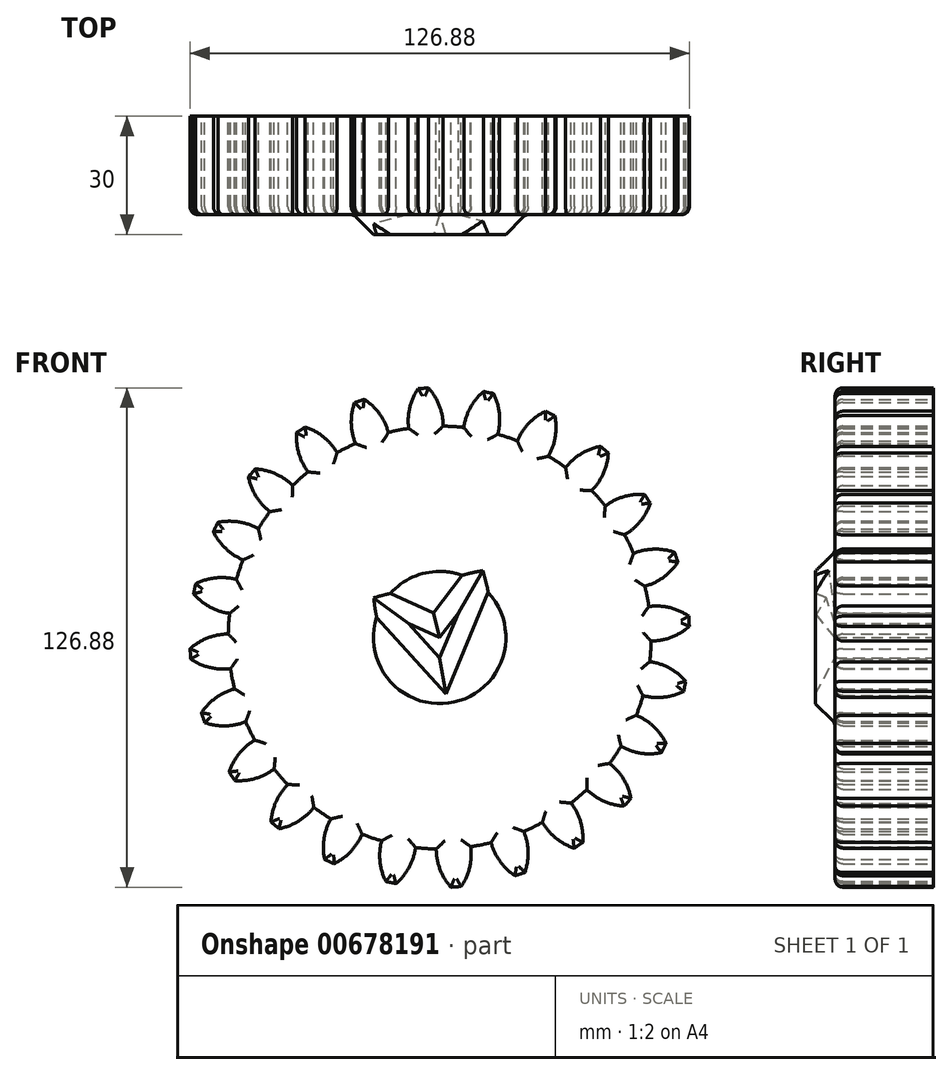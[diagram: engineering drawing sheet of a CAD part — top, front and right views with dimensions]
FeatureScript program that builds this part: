
annotation { "Feature Type Name" : "Feature", "Feature Type Description" : "" }
export const myFeature = defineFeature(function(context is Context, id is Id, definition is map)
    precondition{}
    {
        {
            var Q0;
            Q0=qCreatedBy(makeId("Front.planeOp"),FACE);
            var sketch = newSketch(context, id + "F0", { "sketchPlane" : qUnion([Q0])});
            skCircle(sketch, "E0", {"center": v(0, 0) * mm, "radius": 53.72 * mm});
            skCircle(sketch, "E1", {"center": v(0, 0) * mm, "radius": 58.67 * mm, "construction": true});
            skCircle(sketch, "E2", {"center": v(0, 0) * mm, "radius": 63.5 * mm, "construction": true});
            skLineSegment(sketch, "E3", {"start": v(0, 0) * mm, "end": v(0, 72.49) * mm, "construction": true});
            skLineSegment(sketch, "E4", {"start": v(0, 0) * mm, "end": v(-5.24, 80.02) * mm, "construction": true});
            skLineSegment(sketch, "E5", {"start": v(0, 58.67) * mm, "end": v(-56.45, 58.67) * mm, "construction": true});
            skLineSegment(sketch, "E6", {"start": v(0, 58.67) * mm, "end": v(-56.45, 38.13) * mm, "construction": true});
            skCircle(sketch, "E7", {"center": v(0, 0) * mm, "radius": 55.14 * mm, "construction": true});
            skCircle(sketch, "E8", {"center": v(0, 58.67) * mm, "radius": 14.6 * mm, "construction": true});
            skCircle(sketch, "E9", {"center": v(-13.72, 53.68) * mm, "radius": 14.6 * mm, "construction": true});
            skArc(sketch, "E10", {"start": v(0, 58.67) * mm, "mid": v(-1.2, 61.19) * mm, "end": v(-2.86, 63.44) * mm});
            skArc(sketch, "E11", {"start": v(0.88, 53.71) * mm, "mid": v(0.66, 56.23) * mm, "end": v(0, 58.67) * mm});
            skArc(sketch, "E12.MirrorCS", {"start": v(-7.66, 58.17) * mm, "mid": v(-6.8, 60.82) * mm, "end": v(-5.45, 63.27) * mm});
            skArc(sketch, "E13.MirrorCS", {"start": v(-7.88, 53.14) * mm, "mid": v(-8, 55.67) * mm, "end": v(-7.66, 58.17) * mm});
            skArc(sketch, "E14", {"start": v(-5.45, 63.27) * mm, "mid": v(-4.15, 63.33) * mm, "end": v(-2.86, 63.44) * mm});
            skCircle(sketch, "E15", {"center": v(0, 0) * mm, "radius": 21.8 * mm});
            skLineSegment(sketch, "E16", {"start": v(0, 0) * mm, "end": v(4.78, 6.29) * mm});
            skLineSegment(sketch, "E17", {"start": v(4.78, 6.29) * mm, "end": v(0, -5.17) * mm});
            skLineSegment(sketch, "E18", {"start": v(0, -5.17) * mm, "end": v(-7.89, 3.58) * mm});
            skLineSegment(sketch, "E19", {"start": v(-7.89, 3.58) * mm, "end": v(0, 0) * mm});
            skSolve(sketch);
        }
        {
            var Q0;
            {var subQ0=sQuery(id+"F0.wireOp",EDGE,"E0");var subQ1=makeQuery(id+"F0.imprint","INTERSECT",VERTEX,{"derivedFrom":[subQ0,sQuery(id+"F0.wireOp",EDGE,"E11")]});Q0=makeQuery(id+"F0.imprint","IMPRINT",FACE,{"disambiguationData":[TD([[makeQuery(id+"F0.imprint","IMPRINT",EDGE,{"disambiguationData":[TD([[subQ1,-1.0]])],"derivedFrom":subQ0}),1.0]])]});}
            var Q1;
            Q1=makeQuery(id+"F0.imprint","IMPRINT",FACE,{"disambiguationData":[TD([[makeQuery(id+"F0.imprint","IMPRINT",EDGE,{"derivedFrom":sQuery(id+"F0.wireOp",EDGE,"E10")}),1.0]])]});
            extrude(context, id + "F1", {"entities" : qUnion([Q0, Q1]), "depth" : 25 * mm, "offsetDistance" : 25 * mm});
        }
        {
            var Q0;
            Q0=makeQuery(id+"F1.opExtrude","SWEPT_BODY",BODY,{"disambiguationData":[OSD([sQuery(id+"F0.wireOp",EDGE,"E0"),sQuery(id+"F0.wireOp",EDGE,"E10"),sQuery(id+"F0.wireOp",EDGE,"E11"),sQuery(id+"F0.wireOp",EDGE,"E12.MirrorCS"),sQuery(id+"F0.wireOp",EDGE,"E13.MirrorCS"),sQuery(id+"F0.wireOp",EDGE,"E14")])]});
            var Q1;
            Q1=makeQuery(id+"F1.opExtrude","SWEPT_FACE",FACE,{"disambiguationData":[OSD([sQuery(id+"F0.wireOp",EDGE,"E0")])]});
            circularPattern(context, id + "F2", {"entities" : qUnion([Q0]), "axis" : qUnion([Q1]), "angle" : 360 * degree, "instanceCount" : 24, "equalSpace" : true});
        }
        {
            var Q0;
            Q0=makeQuery(id+"F0.imprint","IMPRINT",FACE,{"disambiguationData":[TD([[makeQuery(id+"F0.imprint","IMPRINT",EDGE,{"derivedFrom":sQuery(id+"F0.wireOp",EDGE,"E15")}),1.0]])]});
            extrude(context, id + "F3", {"entities" : qUnion([Q0]), "operationType" : NewBodyOperationType.ADD, "depth" : 30 * mm, "offsetDistance" : 25 * mm});
        }
        {
            var Q0;
            Q0=makeQuery(id+"F3.opExtrude","CAP_FACE",FACE,{"disambiguationData":[OSD([sQuery(id+"F0.wireOp",EDGE,"E15"),sQuery(id+"F0.wireOp",EDGE,"E16"),sQuery(id+"F0.wireOp",EDGE,"E17"),sQuery(id+"F0.wireOp",EDGE,"E18"),sQuery(id+"F0.wireOp",EDGE,"E19")])],"isStart":false});
            chamfer(context, id + "F4", {"entities" : qUnion([Q0]), "width" : 5 * mm, "tangentPropagation" : true});
        }
        {
            var Q0;
            {var subQ0=makeQuery(id+"F1.opExtrude","CAP_FACE",FACE,{"disambiguationData":[OSD([sQuery(id+"F0.wireOp",EDGE,"E0"),sQuery(id+"F0.wireOp",EDGE,"E10"),sQuery(id+"F0.wireOp",EDGE,"E11"),sQuery(id+"F0.wireOp",EDGE,"E12.MirrorCS"),sQuery(id+"F0.wireOp",EDGE,"E13.MirrorCS"),sQuery(id+"F0.wireOp",EDGE,"E14"),sQuery(id+"F0.wireOp",EDGE,"E15")])],"isStart":false});Q0=makeQuery(id+"F3.boolean.opBoolean","MERGE",FACE,{"derivedFrom":[subQ0,makeQuery(id+"F2.opPattern","COPY",FACE,{"derivedFrom":subQ0,"instanceName":"1"}),makeQuery(id+"F2.opPattern","COPY",FACE,{"derivedFrom":subQ0,"instanceName":"2"}),makeQuery(id+"F2.opPattern","COPY",FACE,{"derivedFrom":subQ0,"instanceName":"3"}),makeQuery(id+"F2.opPattern","COPY",FACE,{"derivedFrom":subQ0,"instanceName":"4"}),makeQuery(id+"F2.opPattern","COPY",FACE,{"derivedFrom":subQ0,"instanceName":"5"}),makeQuery(id+"F2.opPattern","COPY",FACE,{"derivedFrom":subQ0,"instanceName":"6"}),makeQuery(id+"F2.opPattern","COPY",FACE,{"derivedFrom":subQ0,"instanceName":"7"}),makeQuery(id+"F2.opPattern","COPY",FACE,{"derivedFrom":subQ0,"instanceName":"8"}),makeQuery(id+"F2.opPattern","COPY",FACE,{"derivedFrom":subQ0,"instanceName":"9"}),makeQuery(id+"F2.opPattern","COPY",FACE,{"derivedFrom":subQ0,"instanceName":"10"}),makeQuery(id+"F2.opPattern","COPY",FACE,{"derivedFrom":subQ0,"instanceName":"11"}),makeQuery(id+"F2.opPattern","COPY",FACE,{"derivedFrom":subQ0,"instanceName":"12"}),makeQuery(id+"F2.opPattern","COPY",FACE,{"derivedFrom":subQ0,"instanceName":"13"}),makeQuery(id+"F2.opPattern","COPY",FACE,{"derivedFrom":subQ0,"instanceName":"14"}),makeQuery(id+"F2.opPattern","COPY",FACE,{"derivedFrom":subQ0,"instanceName":"15"}),makeQuery(id+"F2.opPattern","COPY",FACE,{"derivedFrom":subQ0,"instanceName":"16"}),makeQuery(id+"F2.opPattern","COPY",FACE,{"derivedFrom":subQ0,"instanceName":"17"}),makeQuery(id+"F2.opPattern","COPY",FACE,{"derivedFrom":subQ0,"instanceName":"18"}),makeQuery(id+"F2.opPattern","COPY",FACE,{"derivedFrom":subQ0,"instanceName":"19"}),makeQuery(id+"F2.opPattern","COPY",FACE,{"derivedFrom":subQ0,"instanceName":"20"}),makeQuery(id+"F2.opPattern","COPY",FACE,{"derivedFrom":subQ0,"instanceName":"21"}),makeQuery(id+"F2.opPattern","COPY",FACE,{"derivedFrom":subQ0,"instanceName":"22"}),makeQuery(id+"F2.opPattern","COPY",FACE,{"derivedFrom":subQ0,"instanceName":"23"})]});}
            fillet(context, id + "F5", {"entities" : qUnion([Q0]), "radius" : 2 * mm, "tangentPropagation" : true, "allowEdgeOverflow" : false});
        }
    });
